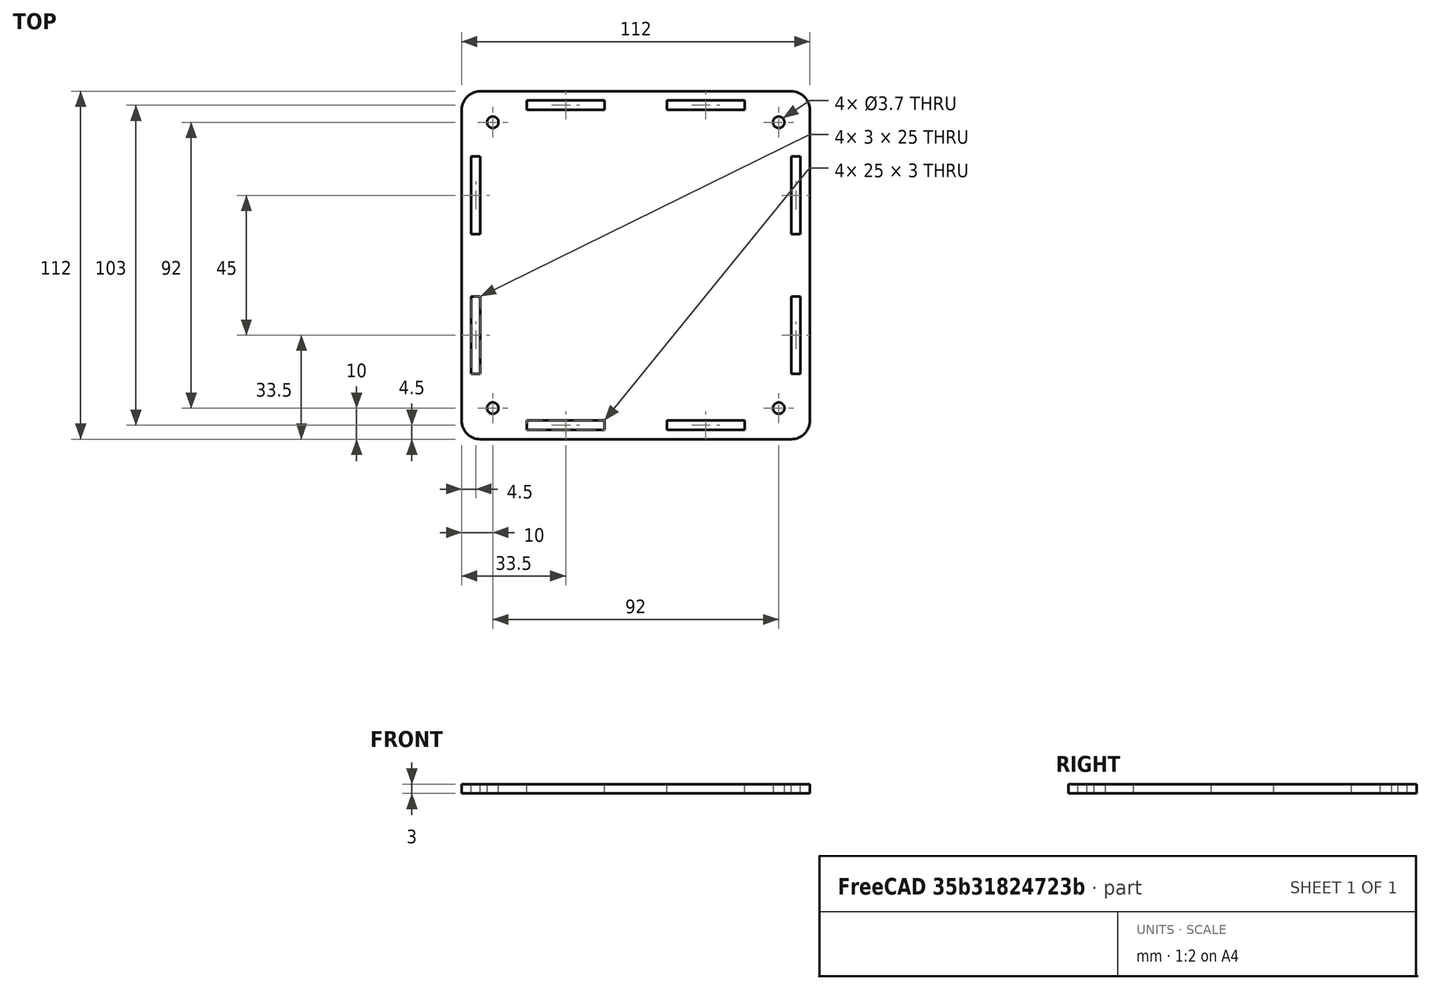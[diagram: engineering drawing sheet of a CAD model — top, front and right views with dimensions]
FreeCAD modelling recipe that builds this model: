
FCSTD DOCUMENT  (FreeCAD 0.19R24267 +99 (Git))
Label: bottom
License: All rights reserved
LicenseURL: http://en.wikipedia.org/wiki/All_rights_reserved
objects: App::Part×1, Sketcher::SketchObject×1, Part::Extrusion×1
note: 2 computed .brp shape members not serialized (recipe doc carries the construction recipe); baked Part::Feature solids carry a one-line shape summary decoded from their .brp

FEATURE [App::Part] Part
  Origin = -> Origin
FEATURE [Sketcher::SketchObject] Sketch
  FullyConstrained = true
  sketch-geometry (48):
    g0: LineSegment StartX=0 StartY=0 StartZ=0 EndX=100 EndY=0 EndZ=0
    g1: LineSegment StartX=100 StartY=0 StartZ=0 EndX=100 EndY=100 EndZ=0
    g2: LineSegment StartX=100 StartY=100 StartZ=0 EndX=0 EndY=100 EndZ=0
    g3: LineSegment StartX=0 StartY=100 StartZ=0 EndX=0 EndY=0 EndZ=0
    g4: ArcOfCircle CenterX=0 CenterY=100 CenterZ=0 NormalX=0 NormalY=0 NormalZ=1 AngleXU=0 Radius=6 StartAngle=1.5708 EndAngle=3.14159
    g5: ArcOfCircle CenterX=100 CenterY=100 CenterZ=0 NormalX=0 NormalY=0 NormalZ=1 AngleXU=0 Radius=6 StartAngle=0 EndAngle=1.5708
    g6: LineSegment StartX=4e-16 StartY=106 StartZ=0 EndX=100 EndY=106 EndZ=0
    g7: Circle CenterX=4 CenterY=96 CenterZ=0 NormalX=0 NormalY=0 NormalZ=1 AngleXU=0 Radius=1.85
    g8: Circle CenterX=96 CenterY=96 CenterZ=0 NormalX=0 NormalY=0 NormalZ=1 AngleXU=0 Radius=1.85
    g9: Circle CenterX=96 CenterY=4 CenterZ=0 NormalX=0 NormalY=0 NormalZ=1 AngleXU=0 Radius=1.85
    g10: Circle CenterX=4 CenterY=4 CenterZ=0 NormalX=0 NormalY=0 NormalZ=1 AngleXU=0 Radius=1.85
    g11: ArcOfCircle CenterX=0 CenterY=0 CenterZ=0 NormalX=0 NormalY=0 NormalZ=1 AngleXU=0 Radius=6 StartAngle=3.14159 EndAngle=4.71239
    g12: ArcOfCircle CenterX=100 CenterY=0 CenterZ=0 NormalX=0 NormalY=0 NormalZ=1 AngleXU=0 Radius=6 StartAngle=4.71239 EndAngle=6.28319
    g13: LineSegment StartX=0 StartY=-6 StartZ=0 EndX=100 EndY=-6 EndZ=0
    g14: LineSegment StartX=106 StartY=-1.5e-15 StartZ=0 EndX=106 EndY=100 EndZ=0
    g15: LineSegment StartX=-6 StartY=100 StartZ=0 EndX=-6 EndY=0 EndZ=0
    g16: LineSegment StartX=15 StartY=100 StartZ=0 EndX=40 EndY=100 EndZ=0
    g17: LineSegment StartX=40 StartY=100 StartZ=0 EndX=40 EndY=103 EndZ=0
    g18: LineSegment StartX=40 StartY=103 StartZ=0 EndX=15 EndY=103 EndZ=0
    g19: LineSegment StartX=15 StartY=103 StartZ=0 EndX=15 EndY=100 EndZ=0
    g20: LineSegment StartX=60 StartY=100 StartZ=0 EndX=85 EndY=100 EndZ=0
    g21: LineSegment StartX=85 StartY=100 StartZ=0 EndX=85 EndY=103 EndZ=0
    g22: LineSegment StartX=85 StartY=103 StartZ=0 EndX=60 EndY=103 EndZ=0
    g23: LineSegment StartX=60 StartY=103 StartZ=0 EndX=60 EndY=100 EndZ=0
    g24: LineSegment StartX=100 StartY=85 StartZ=0 EndX=103 EndY=85 EndZ=0
    g25: LineSegment StartX=103 StartY=85 StartZ=0 EndX=103 EndY=60 EndZ=0
    g26: LineSegment StartX=103 StartY=60 StartZ=0 EndX=100 EndY=60 EndZ=0
    g27: LineSegment StartX=100 StartY=60 StartZ=0 EndX=100 EndY=85 EndZ=0
    g28: LineSegment StartX=100 StartY=40 StartZ=0 EndX=103 EndY=40 EndZ=0
    g29: LineSegment StartX=103 StartY=40 StartZ=0 EndX=103 EndY=15 EndZ=0
    g30: LineSegment StartX=103 StartY=15 StartZ=0 EndX=100 EndY=15 EndZ=0
    g31: LineSegment StartX=100 StartY=15 StartZ=0 EndX=100 EndY=40 EndZ=0
    g32: LineSegment StartX=85 StartY=0 StartZ=0 EndX=60 EndY=0 EndZ=0
    g33: LineSegment StartX=60 StartY=0 StartZ=0 EndX=60 EndY=-3 EndZ=0
    g34: LineSegment StartX=60 StartY=-3 StartZ=0 EndX=85 EndY=-3 EndZ=0
    g35: LineSegment StartX=85 StartY=-3 StartZ=0 EndX=85 EndY=0 EndZ=0
    g36: LineSegment StartX=40 StartY=0 StartZ=0 EndX=15 EndY=0 EndZ=0
    g37: LineSegment StartX=15 StartY=0 StartZ=0 EndX=15 EndY=-3 EndZ=0
    g38: LineSegment StartX=15 StartY=-3 StartZ=0 EndX=40 EndY=-3 EndZ=0
    g39: LineSegment StartX=40 StartY=-3 StartZ=0 EndX=40 EndY=0 EndZ=0
    g40: LineSegment StartX=0 StartY=15 StartZ=0 EndX=-3 EndY=15 EndZ=0
    g41: LineSegment StartX=-3 StartY=15 StartZ=0 EndX=-3 EndY=40 EndZ=0
    g42: LineSegment StartX=-3 StartY=40 StartZ=0 EndX=0 EndY=40 EndZ=0
    g43: LineSegment StartX=0 StartY=40 StartZ=0 EndX=0 EndY=15 EndZ=0
    g44: LineSegment StartX=0 StartY=85 StartZ=0 EndX=-3 EndY=85 EndZ=0
    g45: LineSegment StartX=-3 StartY=85 StartZ=0 EndX=-3 EndY=60 EndZ=0
    g46: LineSegment StartX=-3 StartY=60 StartZ=0 EndX=0 EndY=60 EndZ=0
    g47: LineSegment StartX=0 StartY=60 StartZ=0 EndX=0 EndY=85 EndZ=0
  constraints (143):
    c: Coincident(g0,g1)
    c: Coincident(g1,g2)
    c: Coincident(g2,g3)
    c: Coincident(g3,g0)
    c: Horizontal(g0)
    c: Horizontal(g2)
    c: Vertical(g1)
    c: Vertical(g3)
    c: Coincident(g0,g-1)
    c: DistanceX(g2,g2) = 100
    c: DistanceY(g1,g1) = 100
    c: Coincident(g4,g2)
    c: PointOnObject(g4,g-2)
    c: Horizontal(g4,g4)
    c: Radius(g4) = 6
    c: Coincident(g5,g1)
    c: Radius(g5) = 6
    c: Vertical(g5,g5)
    c: Horizontal(g5,g5)
    c: Coincident(g6,g4)
    c: Coincident(g6,g5)
    c: Equal(g8,g7)
    c: Equal(g7,g10)
    c: Equal(g10,g9)
    c: Radius(g7) = 1.85
    c: Horizontal(g7,g8)
    c: Horizontal(g10,g9)
    c: Vertical(g10,g7)
    c: Vertical(g8,g9)
    c: DistanceX(g4,g7) = 4
    c: DistanceY(g7,g4) = 4
    c: DistanceY(g-1,g10) = 4
    c: DistanceX(g8,g5) = 4
    c: Coincident(g11,g-1)
    c: PointOnObject(g11,g-1)
    c: PointOnObject(g11,g-2)
    c: Radius(g11) = 6
    c: Coincident(g12,g0)
    c: PointOnObject(g12,g-1)
    c: Radius(g12) = 6
    c: Vertical(g12,g12)
    c: Coincident(g13,g11)
    c: Coincident(g13,g12)
    c: Coincident(g14,g12)
    c: Coincident(g14,g5)
    c: Coincident(g15,g4)
    c: Coincident(g15,g11)
    c: Coincident(g16,g17)
    c: Coincident(g17,g18)
    c: Coincident(g18,g19)
    c: Coincident(g19,g16)
    c: Horizontal(g16)
    c: Horizontal(g18)
    c: Vertical(g17)
    c: Vertical(g19)
    c: PointOnObject(g16,g2)
    c: Coincident(g20,g21)
    c: Coincident(g21,g22)
    c: Coincident(g22,g23)
    c: Coincident(g23,g20)
    c: Horizontal(g20)
    c: Horizontal(g22)
    c: Vertical(g21)
    c: Vertical(g23)
    c: PointOnObject(g20,g2)
    c: Coincident(g24,g25)
    c: Coincident(g25,g26)
    c: Coincident(g26,g27)
    c: Coincident(g27,g24)
    c: Horizontal(g24)
    c: Horizontal(g26)
    c: Vertical(g25)
    c: Vertical(g27)
    c: PointOnObject(g24,g1)
    c: Coincident(g28,g29)
    c: Coincident(g29,g30)
    c: Coincident(g30,g31)
    c: Coincident(g31,g28)
    c: Horizontal(g28)
    c: Horizontal(g30)
    c: Vertical(g29)
    c: Vertical(g31)
    c: PointOnObject(g28,g1)
    c: Coincident(g32,g33)
    c: Coincident(g33,g34)
    c: Coincident(g34,g35)
    c: Coincident(g35,g32)
    c: Horizontal(g32)
    c: Horizontal(g34)
    c: Vertical(g33)
    c: Vertical(g35)
    c: PointOnObject(g32,g0)
    c: Coincident(g36,g37)
    c: Coincident(g37,g38)
    c: Coincident(g38,g39)
    c: Coincident(g39,g36)
    c: Horizontal(g36)
    c: Horizontal(g38)
    c: Vertical(g37)
    c: Vertical(g39)
    c: PointOnObject(g36,g0)
    c: Coincident(g40,g41)
    c: Coincident(g41,g42)
    c: Coincident(g42,g43)
    c: Coincident(g43,g40)
    c: Horizontal(g40)
    c: Horizontal(g42)
    c: Vertical(g41)
    c: Vertical(g43)
    c: Coincident(g44,g45)
    c: Coincident(g45,g46)
    c: Coincident(g46,g47)
    c: Coincident(g47,g44)
    c: Horizontal(g44)
    c: Horizontal(g46)
    c: Vertical(g45)
    c: Vertical(g47)
    c: PointOnObject(g44,g3)
    c: Equal(g19,g23)
    c: Equal(g23,g44)
    c: Equal(g44,g24)
    c: Equal(g24,g28)
    c: Equal(g28,g42)
    c: Equal(g42,g39)
    c: Equal(g39,g33)
    c: DistanceY(g39,g39) = 3
    c: Equal(g38,g34)
    c: Equal(g34,g29)
    c: Equal(g29,g41)
    c: Equal(g41,g25)
    c: Equal(g25,g45)
    c: Equal(g45,g18)
    c: Equal(g18,g22)
    c: DistanceX(g18,g18) = 25
    c: DistanceX(g4,g18) = 15
    c: DistanceX(g21,g5) = 15
    c: DistanceY(g24,g5) = 15
    c: DistanceY(g12,g30) = 15
    c: DistanceX(g34,g12) = 15
    c: DistanceX(g11,g37) = 15
    c: DistanceY(g11,g40) = 15
    c: DistanceY(g44,g4) = 15
    c: PointOnObject(g40,g3)
FEATURE [Part::Extrusion] Extrude
  Base = -> Sketch
  Dir = (0,0,1)
  DirMode = 2
  FaceMakerClass = Part::FaceMakerBullseye
  LengthFwd = 3
  LengthRev = 0
  Solid = true
  Symmetric = false
